# Revit family: Дверь РДО1
name_source: partatom
category: Двери
revit_build: Autodesk Revit 2015 (Build: 20140223_1515(x64)
units: mm (PartAtom-declared; Revit-internal decimal feet)

## types (1)
- Дверь РДО
    ADSK_URL страницы изделия = http://profholod.ru
    ADSK_Завод-изготовитель = ООО ПрофХолод
    ADSK_Обозначение = ООО ПрофХолод
    ADSK_Открывание = Лев
    AISI = AISI430
    H порога = 80 мм
    RAL = RAL
    URL = http://profholod.ru
    a = 80 мм
    b = 90 мм
    c = 90 мм
    Аналитическая конструкция = <Нет>
    Внутренняя сторона = RAL9003
    Высота = 1900 мм
    Высота порога = 80 мм
    Высота проема до монтажа = 1900 мм
    Высота ручки = 900 мм
    Группа модели = РДО
    Замыкание стены = По основе
    Изготовитель = ООО ПрофХолод
    Кирпич = ККС : КРК - к крипичной стене
    Металл = ККС : МК - к металлоконструкции
    НЕТ = НЕТ
    Наружная сторона = RAL9003
    Описание = Дверь холодильная
    Петли левые = Да
    Петли смещение = 160 мм
    Петли справа = Нет
    Пластиковые накладки = РДОП пластик
    Полотно без порога = Нет
    Полотно с порогом = Да
    Порог = Да
    Рама = AISI 304-0,5
    Рама_сечение = 106 мм
    Сендвич = ККС : СП - к сэндвич-панели
    Толщина полотна = 80 мм
    Уплотнитель = РДОП уплотнитель
    Функция = Внутренние слои
    Ширина = 800 мм
    Ширина полотна = 900 мм
    Ширина проема до монтажа = 800 мм
    пНЕРЖ = Порог : AISI430
    пНЕТ = Порог : NULL
    пРАЛ = Порог : RAL 9003
